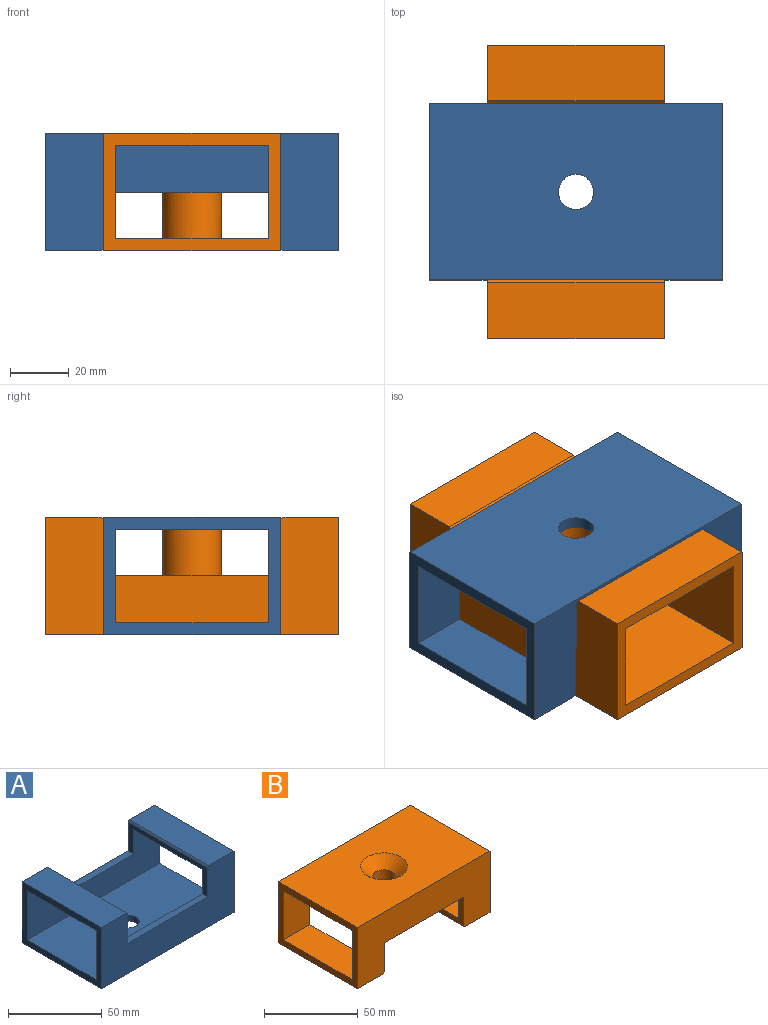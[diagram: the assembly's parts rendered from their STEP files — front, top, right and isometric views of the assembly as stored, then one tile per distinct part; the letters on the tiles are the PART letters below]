
ASSEMBLY  parts=2 mates=1
PART A: 19 faces, bbox 100x60x40 mm
  f0: plane 60x19mm, normal (0,0,1), area 1140mm2, adj f2,f4,f10,f18
  f1: plane 52x20mm, normal (0,0,-1), area 1040mm2, adj f6,f8,f11,f14
  f2: plane 100x40mm, normal (0,-1,0), area 2799mm2, adj f0,f3,f5,f10,f11,f12,f13,f14
  f3: plane 100x60mm, normal (0,0,-1), area 5886.9mm2, adj f2,f4,f10,f11,f16
  f4: plane 100x40mm, normal (0,1,0), area 2799mm2, adj f0,f3,f5,f10,f11,f13,f14,f15
  f5: plane 60x19mm, normal (0,0,1), area 1140mm2, adj f2,f4,f11,f17
  f6: plane 100x32mm, normal (0,-1,0), area 2240mm2, adj f1,f7,f9,f10,f11,f13,f14,f15
  f7: plane 100x52mm, normal (0,0,1), area 5086.9mm2, adj f6,f8,f10,f11,f16
  f8: plane 100x32mm, normal (0,1,0), area 2240mm2, adj f1,f7,f9,f10,f11,f12,f13,f14
  f9: plane 52x20mm, normal (0,0,-1), area 1040mm2, adj f6,f8,f10,f13
  f10: plane 60x40mm, normal (1,0,0), area 736mm2, adj f0,f2,f3,f4,f6,f7,f8,f9
  f11: plane 60x40mm, normal (-1,0,0), area 736mm2, adj f1,f2,f3,f4,f5,f6,f7,f8
  f12: plane 60x4mm, normal (0,0,1), area 240mm2, adj f2,f8,f13,f14
  f13: plane 60x19mm, normal (-1,0,0), area 308mm2, adj f2,f4,f6,f8,f9,f12,f15,f18
  f14: plane 60x19mm, normal (1,0,0), area 308mm2, adj f1,f2,f4,f6,f8,f12,f15,f17
  f15: plane 60x4mm, normal (0,0,1), area 240mm2, adj f4,f6,f13,f14
  f16: cylinder r=6mm len=12mm, axis (0,0,-1), area 150.8mm2, adj f3,f7
  f17: plane 60x1mm, normal (0.71,0,0.71), area 84.9mm2, adj f2,f4,f5,f14
  f18: plane 60x1mm, normal (-0.71,0,0.71), area 84.9mm2, adj f0,f2,f4,f13
PART B: 22 faces, bbox 100x60x40 mm
  f0: plane 52x20mm, normal (0,0,1), area 1040mm2, adj f4,f9,f11,f16
  f1: plane 100x40mm, normal (0,-1,0), area 2799mm2, adj f2,f6,f8,f10,f11,f16,f17,f18
  f2: plane 60x19mm, normal (0,0,-1), area 1140mm2, adj f1,f7,f10,f20
  f3: plane 52x20mm, normal (0,0,1), area 1040mm2, adj f4,f9,f10,f17
  f4: plane 100x32mm, normal (0,1,0), area 2240mm2, adj f0,f3,f5,f10,f11,f16,f17,f18
  f5: plane 100x52mm, normal (0,0,-1), area 4885.8mm2, adj f4,f9,f10,f11,f12
  f6: plane 60x19mm, normal (0,0,-1), area 1140mm2, adj f1,f7,f11,f21
  f7: plane 100x40mm, normal (0,1,0), area 2799mm2, adj f2,f6,f8,f10,f11,f15,f16,f17
  f8: plane 100x60mm, normal (0,0,1), area 5509.1mm2, adj f1,f7,f10,f11,f14
  f9: plane 100x32mm, normal (0,-1,0), area 2240mm2, adj f0,f3,f5,f10,f11,f15,f16,f17
  f10: plane 60x40mm, normal (1,0,0), area 736mm2, adj f1,f2,f3,f4,f5,f7,f8,f9
  f11: plane 60x40mm, normal (-1,0,0), area 736mm2, adj f0,f1,f4,f5,f6,f7,f8,f9
  f12: cylinder r=10mm len=32mm, axis (0,0,-1), area 2010.6mm2, adj f5,f19
  f13: cylinder r=6mm len=29.5mm, axis (0,0,1), area 1112.1mm2, adj f14,f19
  f14: cone r=6mm half-angle=45deg, axis (0,0,1), area 534.3mm2, adj f8,f13
  f15: plane 60x4mm, normal (0,0,-1), area 240mm2, adj f7,f9,f16,f17
  f16: plane 60x19mm, normal (1,0,0), area 308mm2, adj f0,f1,f4,f7,f9,f15,f18,f21
  f17: plane 60x19mm, normal (-1,0,0), area 308mm2, adj f1,f3,f4,f7,f9,f15,f18,f20
  f18: plane 60x4mm, normal (0,0,-1), area 240mm2, adj f1,f4,f16,f17
  f19: plane 20x20mm, normal (0,0,-1), area 201.1mm2, adj f12,f13
  f20: plane 60x1mm, normal (-0.71,0,-0.71), area 84.9mm2, adj f1,f2,f7,f17
  f21: plane 60x1mm, normal (0.71,0,-0.71), area 84.9mm2, adj f1,f6,f7,f16
PLACE A rot(axis=(0,1,0),180deg) t=(80,48.4,20)mm
PLACE B rot(axis=(0.71,0.71,0),180deg) t=(30,-100,20)mm
MATE fastened B.f13 <-> A.f16  axis (0,0,-1) through (30,-50,36)mm
